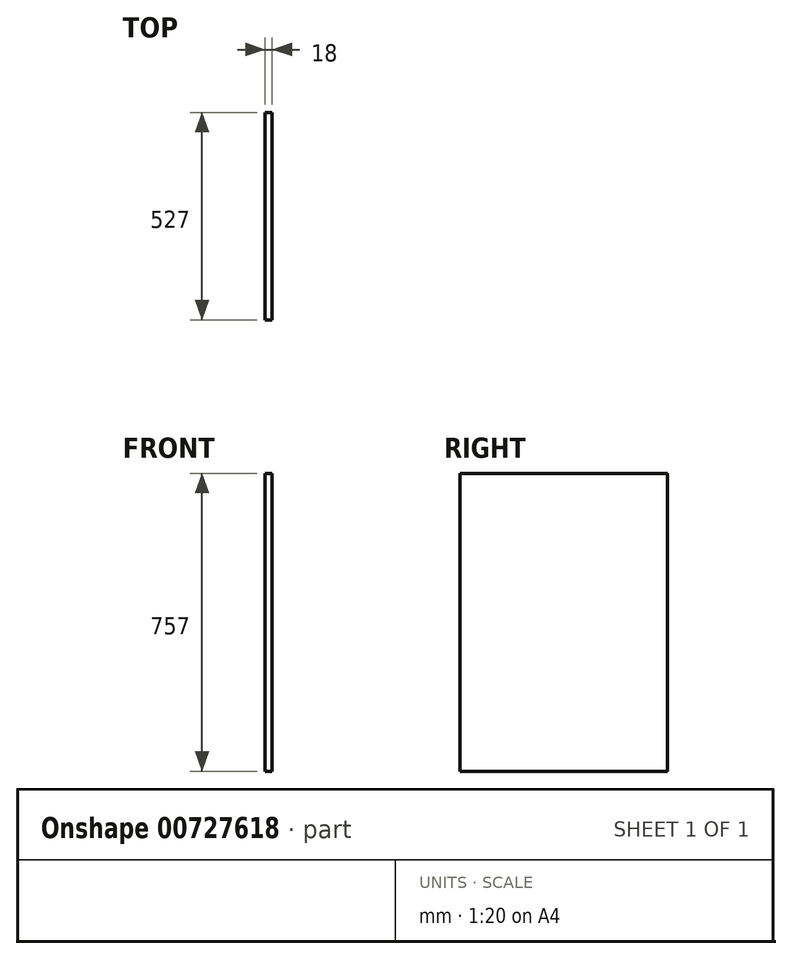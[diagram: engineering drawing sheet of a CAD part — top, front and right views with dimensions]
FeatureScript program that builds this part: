
annotation { "Feature Type Name" : "Feature", "Feature Type Description" : "" }
export const myFeature = defineFeature(function(context is Context, id is Id, definition is map)
    precondition{}
    {
        {
            var Q0;
            Q0=qCreatedBy(makeId("Right.planeOp"),FACE);
            var sketch = newSketch(context, id + "F0", { "sketchPlane" : qUnion([Q0])});
            skLineSegment(sketch, "E0.bottom", {"start": v(-263.5, 378.5) * mm, "end": v(263.5, 378.5) * mm});
            skLineSegment(sketch, "E0.top", {"start": v(-263.5, -378.5) * mm, "end": v(263.5, -378.5) * mm});
            skLineSegment(sketch, "E0.left", {"start": v(-263.5, 378.5) * mm, "end": v(-263.5, -378.5) * mm});
            skLineSegment(sketch, "E0.right", {"start": v(263.5, 378.5) * mm, "end": v(263.5, -378.5) * mm});
            skLineSegment(sketch, "E1", {"start": v(-263.5, 378.5) * mm, "end": v(263.5, -378.5) * mm, "construction": true});
            skSolve(sketch);
        }
        {
            var Q0;
            Q0 = qSketchRegion(id + "F0", true);
            extrude(context, id + "F1", {"entities" : qUnion([Q0]), "depth" : 18 * mm, "offsetDistance" : 25 * mm});
        }
    });
